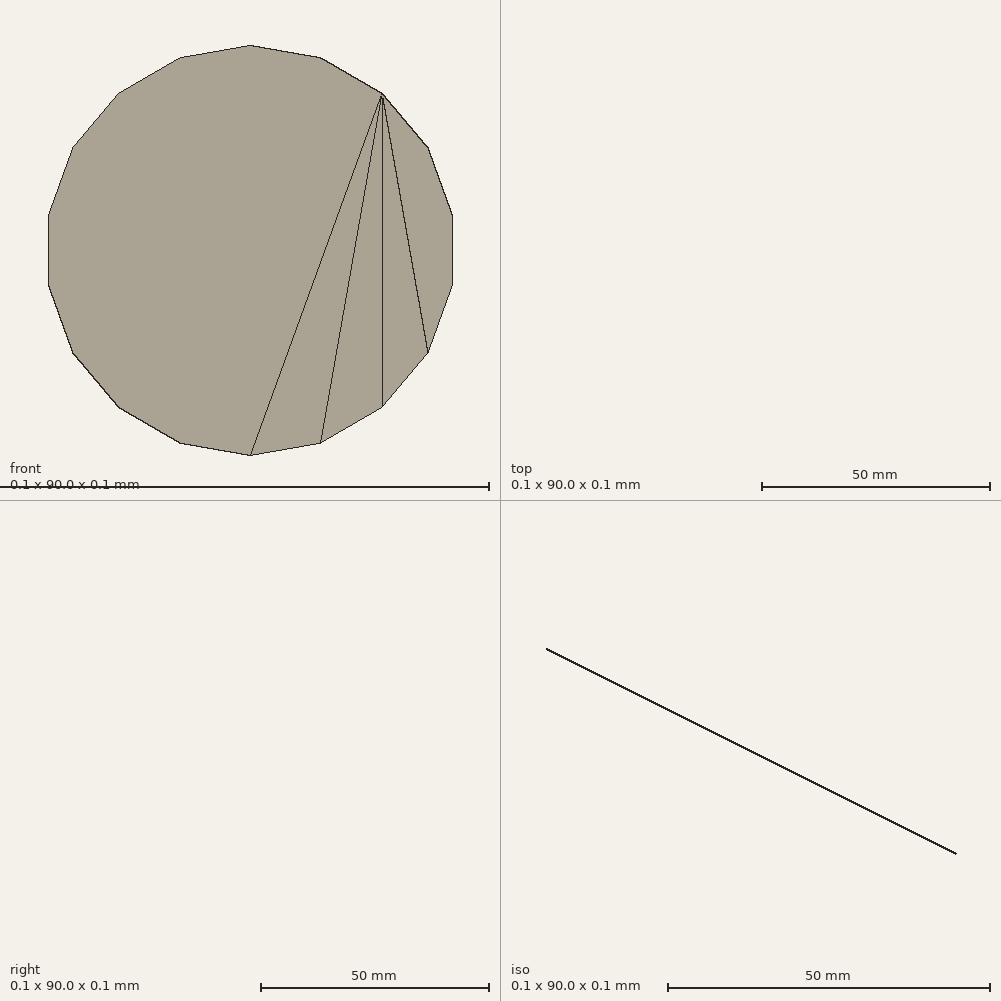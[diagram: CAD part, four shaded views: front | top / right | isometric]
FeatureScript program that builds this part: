
annotation { "Feature Type Name" : "Feature", "Feature Type Description" : "" }
export const myFeature = defineFeature(function(context is Context, id is Id, definition is map)
    precondition{}
    {
        {
            var Q0;
            Q0=qCreatedBy(makeId("Front.planeOp"),FACE);
            var sketch = newSketch(context, id + "F0", { "sketchPlane" : qUnion([Q0])});
            skCircle(sketch, "E0", {"center": v(0, 0) * mm, "radius": 0.05 * mm});
            skSolve(sketch);
        }
        {
            var Q0;
            Q0=qSketchRegion(id+"F0",true);
            extrude(context, id + "F1", {"entities" : qUnion([Q0]), "depth" : 90 * mm, "offsetDistance" : 25 * mm});
        }
    });
